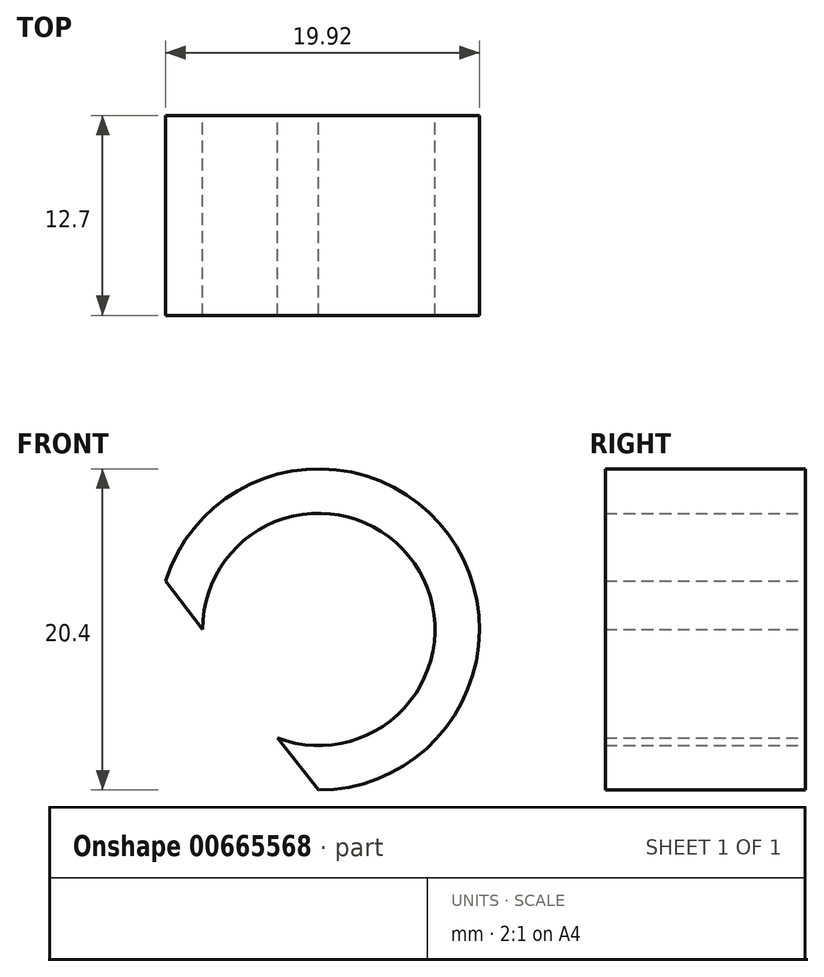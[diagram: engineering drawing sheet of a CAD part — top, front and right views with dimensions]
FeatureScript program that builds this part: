
annotation { "Feature Type Name" : "Feature", "Feature Type Description" : "" }
export const myFeature = defineFeature(function(context is Context, id is Id, definition is map)
    precondition{}
    {
        {
            var Q0;
            Q0=qCreatedBy(makeId("Front.planeOp"),FACE);
            var sketch = newSketch(context, id + "F0", { "sketchPlane" : qUnion([Q0])});
            skArc(sketch, "E0", {"start": v(0, 0) * mm, "mid": v(8.23, 16.22) * mm, "end": v(-9.72, 13.3) * mm});
            skArc(sketch, "E1", {"start": v(-2.62, 3.3) * mm, "mid": v(6.07, 14.4) * mm, "end": v(-7.38, 10.2) * mm});
            skLineSegment(sketch, "E2", {"start": v(-9.72, 13.3) * mm, "end": v(-7.38, 10.2) * mm});
            skLineSegment(sketch, "E3", {"start": v(-2.62, 3.3) * mm, "end": v(0, 0) * mm});
            skSolve(sketch);
        }
        {
            var Q0;
            Q0 = qSketchRegion(id + "F0", true);
            extrude(context, id + "F1", {"entities" : qUnion([Q0]), "endBound" : BoundingType.SYMMETRIC, "depth" : 12.7 * mm, "offsetDistance" : 25.4 * mm});
        }
    });
